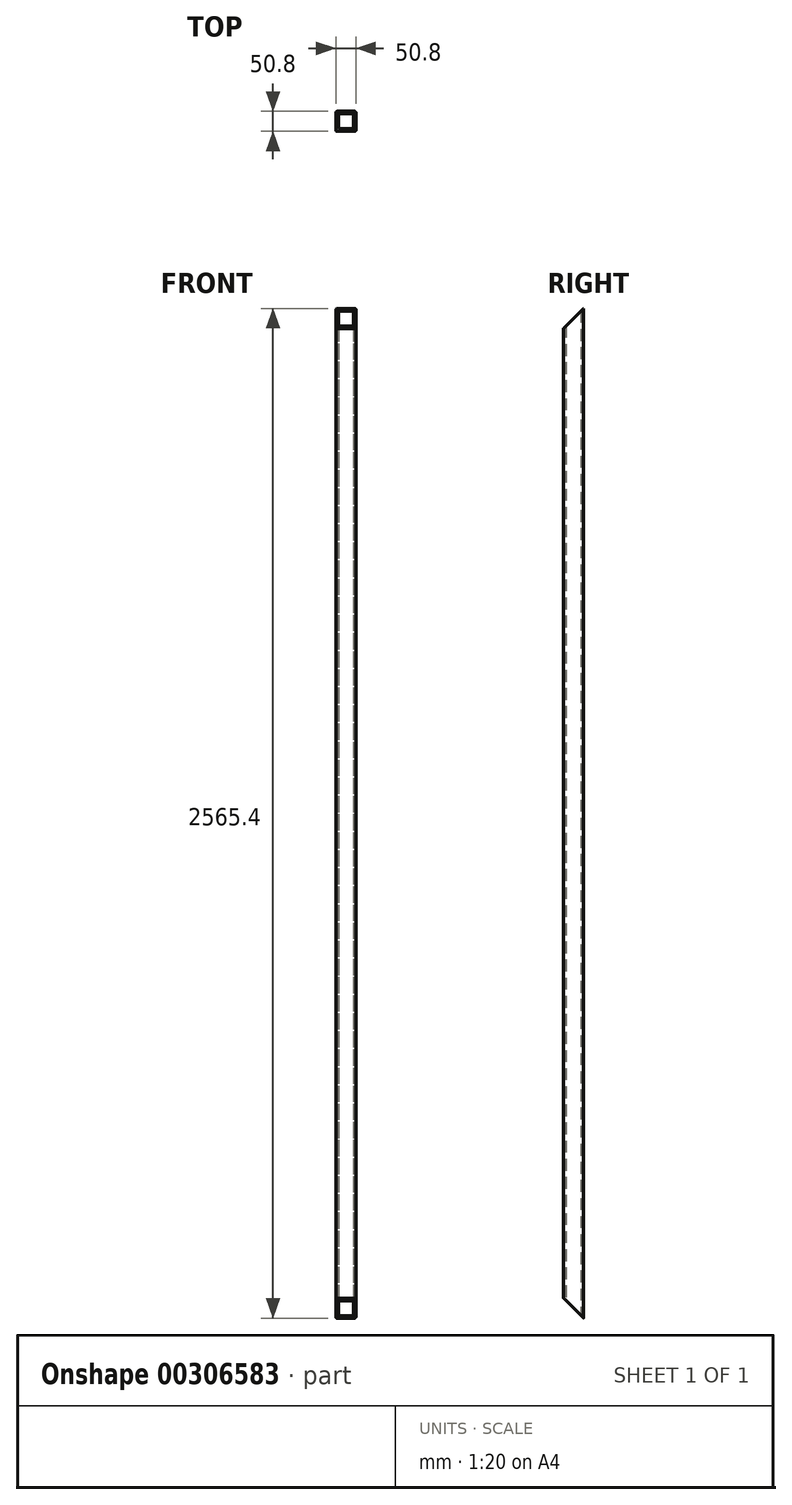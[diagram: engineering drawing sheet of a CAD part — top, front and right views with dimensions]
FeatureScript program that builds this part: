
annotation { "Feature Type Name" : "Feature", "Feature Type Description" : "" }
export const myFeature = defineFeature(function(context is Context, id is Id, definition is map)
    precondition{}
    {
        {
            var Q0;
            Q0=qCreatedBy(makeId("Top.planeOp"),FACE);
            var sketch = newSketch(context, id + "F0", { "sketchPlane" : qUnion([Q0])});
            skLineSegment(sketch, "E0.bottom", {"start": v(-22.22, 25.4) * mm, "end": v(22.23, 25.4) * mm});
            skLineSegment(sketch, "E0.top", {"start": v(-22.23, -25.4) * mm, "end": v(22.23, -25.4) * mm});
            skLineSegment(sketch, "E0.left", {"start": v(-25.4, 22.22) * mm, "end": v(-25.4, -22.23) * mm});
            skLineSegment(sketch, "E0.right", {"start": v(25.4, 22.22) * mm, "end": v(25.4, -22.23) * mm});
            skPoint(sketch, "E0.middle", {"position": v(0, 0) * mm});
            skPoint(sketch, "E1.visualSharp", {"position": v(-25.4, 25.4) * mm});
            skArc(sketch, "E1.filletArc", {"start": v(-22.22, 25.4) * mm, "mid": v(-24.47, 24.47) * mm, "end": v(-25.4, 22.22) * mm});
            skPoint(sketch, "E2.visualSharp", {"position": v(-25.4, -25.4) * mm});
            skArc(sketch, "E2.filletArc", {"start": v(-25.4, -22.23) * mm, "mid": v(-24.47, -24.47) * mm, "end": v(-22.23, -25.4) * mm});
            skPoint(sketch, "E3.visualSharp", {"position": v(25.4, -25.4) * mm});
            skArc(sketch, "E3.filletArc", {"start": v(22.23, -25.4) * mm, "mid": v(24.47, -24.47) * mm, "end": v(25.4, -22.23) * mm});
            skPoint(sketch, "E4.visualSharp", {"position": v(25.4, 25.4) * mm});
            skArc(sketch, "E4.filletArc", {"start": v(25.4, 22.22) * mm, "mid": v(24.47, 24.47) * mm, "end": v(22.23, 25.4) * mm});
            skLineSegment(sketch, "E5.0", {"start": v(-17.46, 19.05) * mm, "end": v(17.46, 19.05) * mm});
            skLineSegment(sketch, "E5.1", {"start": v(-19.05, 17.46) * mm, "end": v(-19.05, -17.46) * mm});
            skLineSegment(sketch, "E5.2", {"start": v(-17.46, -19.05) * mm, "end": v(17.46, -19.05) * mm});
            skLineSegment(sketch, "E5.3", {"start": v(19.05, 17.46) * mm, "end": v(19.05, -17.46) * mm});
            skPoint(sketch, "E6.visualSharp", {"position": v(-19.05, 19.05) * mm});
            skArc(sketch, "E6.filletArc", {"start": v(-17.46, 19.05) * mm, "mid": v(-18.59, 18.59) * mm, "end": v(-19.05, 17.46) * mm});
            skPoint(sketch, "E7.visualSharp", {"position": v(-19.05, -19.05) * mm});
            skArc(sketch, "E7.filletArc", {"start": v(-19.05, -17.46) * mm, "mid": v(-18.59, -18.59) * mm, "end": v(-17.46, -19.05) * mm});
            skPoint(sketch, "E8.visualSharp", {"position": v(19.05, -19.05) * mm});
            skArc(sketch, "E8.filletArc", {"start": v(17.46, -19.05) * mm, "mid": v(18.59, -18.59) * mm, "end": v(19.05, -17.46) * mm});
            skPoint(sketch, "E9.visualSharp", {"position": v(19.05, 19.05) * mm});
            skArc(sketch, "E9.filletArc", {"start": v(19.05, 17.46) * mm, "mid": v(18.59, 18.59) * mm, "end": v(17.46, 19.05) * mm});
            skSolve(sketch);
        }
        {
            var Q0;
            Q0=makeQuery(id+"F0.imprint","IMPRINT",FACE,{"disambiguationData":[TD([[makeQuery(id+"F0.imprint","IMPRINT",EDGE,{"derivedFrom":sQuery(id+"F0.wireOp",EDGE,"E0.bottom")}),-1.0]])]});
            extrude(context, id + "F1", {"entities" : qUnion([Q0]), "depth" : 2565.4 * mm});
        }
        {
            var Q0;
            Q0=makeQuery(id+"F1.opExtrude","SWEPT_FACE",FACE,{"disambiguationData":[OSD([sQuery(id+"F0.wireOp",EDGE,"E0.right")])]});
            var sketch = newSketch(context, id + "F2", { "sketchPlane" : qUnion([Q0])});
            skLineSegment(sketch, "E10", {"start": v(25.4, 2565.4) * mm, "end": v(-25.4, 2514.6) * mm});
            skLineSegment(sketch, "E11", {"start": v(-25.4, 2514.6) * mm, "end": v(-25.4, 2565.4) * mm});
            skLineSegment(sketch, "E12", {"start": v(-25.4, 2565.4) * mm, "end": v(25.4, 2565.4) * mm});
            skLineSegment(sketch, "E13", {"start": v(25.4, 0) * mm, "end": v(-25.4, 50.8) * mm});
            skLineSegment(sketch, "E14", {"start": v(-25.4, 50.8) * mm, "end": v(-25.4, 0) * mm});
            skLineSegment(sketch, "E15", {"start": v(-25.4, 0) * mm, "end": v(25.4, 0) * mm});
            skSolve(sketch);
        }
        {
            var Q0;
            Q0=qSketchRegion(id+"F2",true);
            extrude(context, id + "F3", {"entities" : qUnion([Q0]), "operationType" : NewBodyOperationType.REMOVE, "endBound" : BoundingType.THROUGH_ALL, "oppositeDirection" : true, "depth" : 25.4 * mm});
        }
    });
